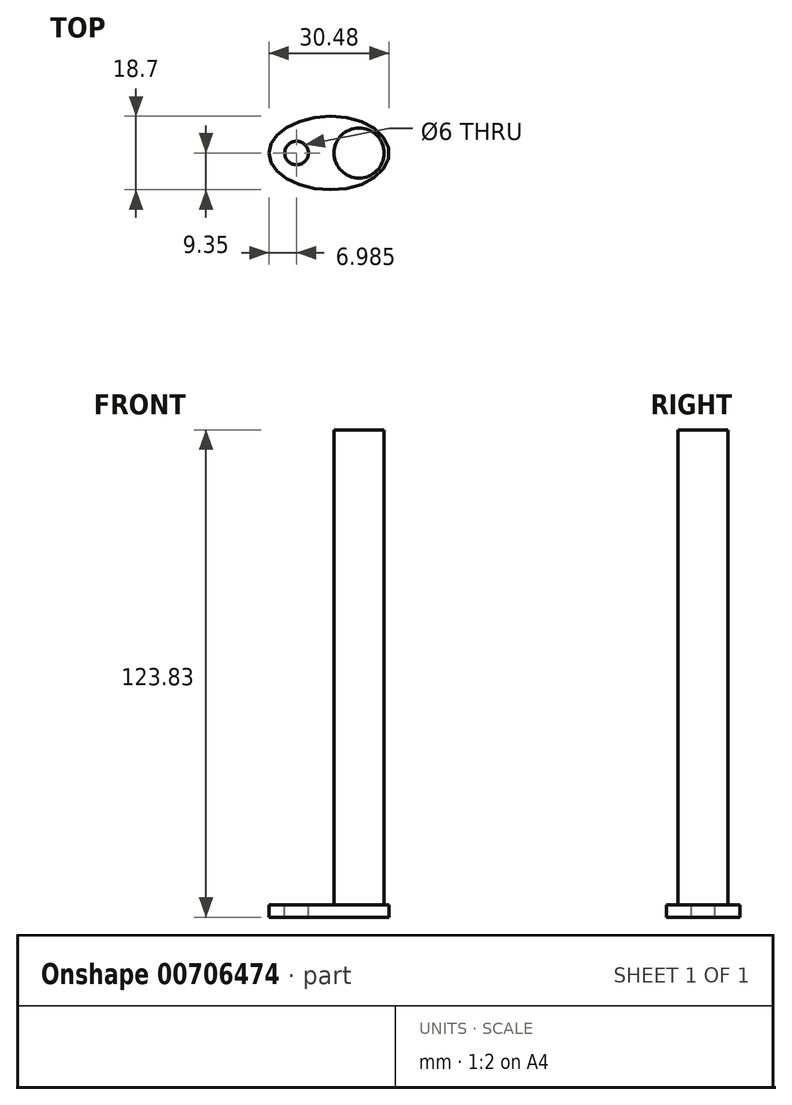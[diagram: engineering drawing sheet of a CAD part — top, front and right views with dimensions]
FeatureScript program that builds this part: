
annotation { "Feature Type Name" : "Feature", "Feature Type Description" : "" }
export const myFeature = defineFeature(function(context is Context, id is Id, definition is map)
    precondition{}
    {
        {
            var Q0;
            Q0=qCreatedBy(makeId("Top.planeOp"),FACE);
            var sketch = newSketch(context, id + "F0", { "sketchPlane" : qUnion([Q0])});
            skCircle(sketch, "E0", {"center": v(0, 0) * mm, "radius": 6.35 * mm});
            skSolve(sketch);
        }
        {
            var Q0;
            Q0=makeQuery(id+"F0.imprint","IMPRINT",FACE,{"disambiguationData":[TD([[makeQuery(id+"F0.imprint","IMPRINT",EDGE,{"derivedFrom":sQuery(id+"F0.wireOp",EDGE,"E0")}),1.0]])]});
            extrude(context, id + "F1", {"entities" : qUnion([Q0]), "depth" : 120.65 * mm, "offsetDistance" : 25.4 * mm});
        }
        {
            var Q0;
            Q0=qCreatedBy(makeId("Top.planeOp"),FACE);
            var sketch = newSketch(context, id + "F2", { "sketchPlane" : qUnion([Q0])});
            skFitSpline(sketch, "E1", {"points": [v(-22.86, 0) * mm, v(-17.78, 6.86) * mm, v(0, 8.26) * mm, v(7.62, 0) * mm, v(0, -8.26) * mm, v(-17.78, -6.86) * mm, v(-22.86, 0) * mm]});
            skLineSegment(sketch, "E2", {"start": v(-17.78, 0) * mm, "end": v(-17.78, 6.86) * mm, "construction": true});
            skLineSegment(sketch, "E3", {"start": v(-17.78, 0) * mm, "end": v(-17.78, -6.86) * mm, "construction": true});
            skLineSegment(sketch, "E4", {"start": v(-17.78, 0) * mm, "end": v(-22.86, 0) * mm, "construction": true});
            skLineSegment(sketch, "E5", {"start": v(7.62, 0) * mm, "end": v(0, 0) * mm, "construction": true});
            skLineSegment(sketch, "E6", {"start": v(0, 0) * mm, "end": v(0, 8.26) * mm, "construction": true});
            skLineSegment(sketch, "E7", {"start": v(0, 0) * mm, "end": v(0, -8.26) * mm, "construction": true});
            skLineSegment(sketch, "E8", {"start": v(0, 0) * mm, "end": v(-17.78, 0) * mm, "construction": true});
            skCircle(sketch, "E9", {"center": v(-15.88, 0) * mm, "radius": 3 * mm});
            skSolve(sketch);
        }
        {
            var Q0;
            Q0=makeQuery(id+"F2.imprint","IMPRINT",FACE,{"disambiguationData":[TD([[makeQuery(id+"F2.imprint","IMPRINT",EDGE,{"derivedFrom":sQuery(id+"F2.wireOp",EDGE,"E1")}),-1.0]])]});
            extrude(context, id + "F3", {"entities" : qUnion([Q0]), "operationType" : NewBodyOperationType.ADD, "depth" : -3.17 * mm, "offsetDistance" : 25.4 * mm});
        }
    });
